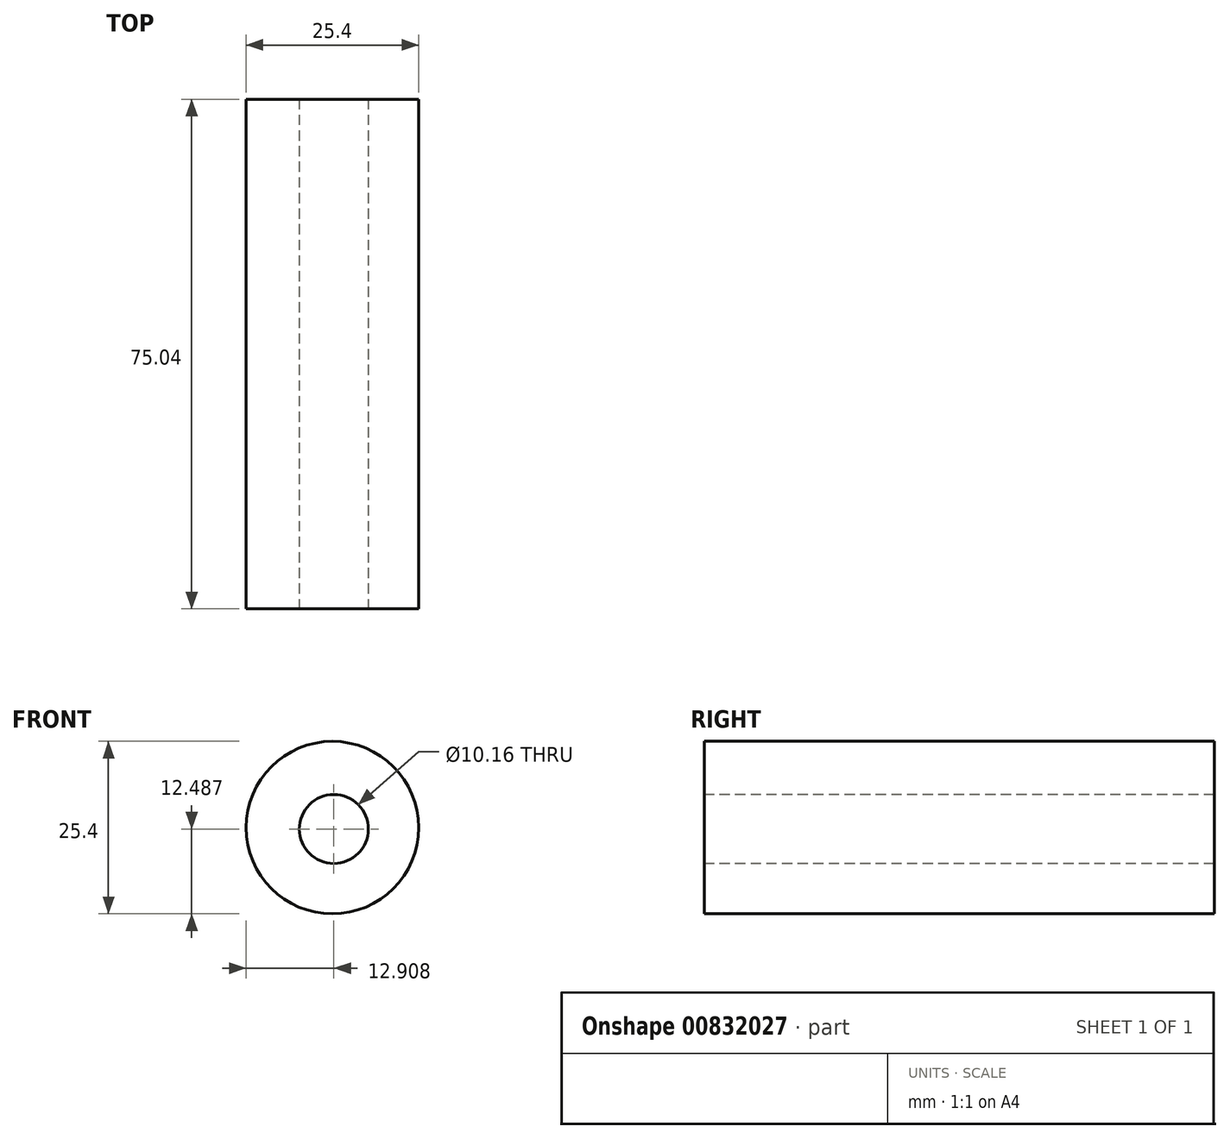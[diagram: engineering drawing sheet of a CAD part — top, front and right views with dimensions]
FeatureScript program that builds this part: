
annotation { "Feature Type Name" : "Feature", "Feature Type Description" : "" }
export const myFeature = defineFeature(function(context is Context, id is Id, definition is map)
    precondition{}
    {
        {
            var Q0;
            Q0=qCreatedBy(makeId("Front.planeOp"),FACE);
            var sketch = newSketch(context, id + "F0", { "sketchPlane" : qUnion([Q0])});
            skCircle(sketch, "E0", {"center": v(-37.55, 20.75) * mm, "radius": 12.7 * mm});
            skCircle(sketch, "E1", {"center": v(-37.34, 20.54) * mm, "radius": 5.08 * mm});
            skPoint(sketch, "E1.first.point", {"position": v(-42.42, 20.75) * mm});
            skPoint(sketch, "E1.second.point", {"position": v(-32.27, 20.75) * mm});
            skPoint(sketch, "E1.third.point", {"position": v(-37.55, 25.61) * mm});
            skLineSegment(sketch, "E2", {"start": v(-24.85, 20.75) * mm, "end": v(-32.27, 20.75) * mm});
            skLineSegment(sketch, "E3", {"start": v(-50.25, 20.75) * mm, "end": v(-42.42, 20.75) * mm});
            skLineSegment(sketch, "E4", {"start": v(-35.16, 33.22) * mm, "end": v(-37.55, 25.61) * mm});
            skLineSegment(sketch, "E5", {"start": v(-37.34, 8.05) * mm, "end": v(-37.34, 15.46) * mm});
            skSolve(sketch);
        }
        {
            var Q0;
            Q0 = qSketchRegion(id + "F0", true);
            extrude(context, id + "F1", {"entities" : qUnion([Q0]), "oppositeDirection" : true, "depth" : 75.04 * mm, "offsetDistance" : 25.4 * mm});
        }
    });
